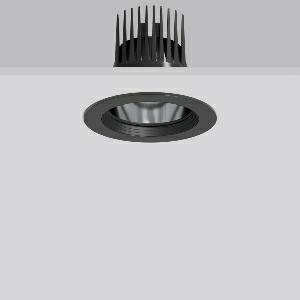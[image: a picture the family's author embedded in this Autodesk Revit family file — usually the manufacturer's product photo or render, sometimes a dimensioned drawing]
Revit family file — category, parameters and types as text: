
# Revit family: heledon_maxi_e_901756_003_8b9c
name_source: partatom
category: Lighting Fixtures
units: mm (PartAtom-declared; Revit-internal decimal feet)

## family parameters
Cut with Voids When Loaded = No
Host = Face
Light Source = No
Part Type = Normal
Room Calculation Point = No
Round Connector Dimension = Use Diameter
Shared = No

## types (1)
- HELEDON maxi E (1 x LED Modul 930, 3250 lm, 3000)
    Apparent Load = 25 VA
    Approval mark = CE
    CIE Flux Codes = 100 100 100 100 100
    Color Rendering = 90
    Color Temperature = 3000
    Default Elevation = 1800 mm
    Description = Series: HELEDON maxi
Round recessed downlight. Housing: die-cast aluminium, powder-coated. Black plastic ring and recessed LED to prevent glare from the side. Optical assembly with reflector made of MIRO-Silver with 98% total light reflection for outstanding efficiency - can be changed without tools. Best colour rendering index Ra>90. Suitable for Recessed ceiling mounting. Installation without tools thanks to spring fastening system. Including separate LED converter with connecting cable 600 mm.High quality converter without flickering and stroboscopic effect. Through-wiring box (5 pole) available as accessory. The following accessories can be mounted without use of tools: interchangeable lenses, decorative glasses, honeycomb louvre, clear and frosted diffusers, white interchangeable plastic ring. 
Colour: deep black, matt (RAL 9005)
Diameter: 162 mm
Height: 3 mm
Cut-out diameter: 152 mm
Recess height: 200 mm
Luminaire: recess height: 135 mm
Lamp: LED
Socket: without socket
Colour temperature: 3000K
Colour rendering index (CRI): 92
System power: 25 W
Rated luminous flux: 3250 lm
Luminous efficiency: 130 lm/W
Control gear: Regulated power supply
Protection class: II
Type of protection: IP 20
    Height = 0 mm  [stored 0 ft]
    Lamp = 1 x LED Modul 930
    Lamp Light Flux = 3250 lm
    Lamp count = 1
    Length = 162 mm
    Lifetime = 50000 h
    Luminous efficacy = 130 lm/W
    Manufacturer = RZB
    ModVariant = No
    Model = 901756.003
    Mounting Place = Ceiling
    Mounting Type = Recessed
    Number of Poles = 1
    OnlyDefault = Yes
    Power Factor = 1
    Product Name = HELEDON maxi E
    Product group = Recessed downlights
    ProductGroupID = 402
    Protection Class = Protection class II
    Protection Degree = IP 20
    RLX_Detail_Level = 1
    RLX_Emergency_Light_Flux = 0 lm
    RLX_Emergency_Type = 0
    RLX_Emergency_Type_DB = No
    RlxData = <blob elided: 121321 chars, md5=615be974>
    Socket = socket
    Standby Power = 0 W
    System Light Flux = 3250 lm
    System Power = 25 W
    Type Comments = Product without accessories
    Type Image = 901662.003.jpg
    URL = http://relux.com
    VarID = ---
    Voltage = 230 V
    Voltage Range = 220-240 V
    Weight = 0.00 kg
    Width = 0 mm  [stored 0 ft]

note: [stored X ft] marks values corroborated as IEEE doubles in the binary element streams (Revit-internal decimal feet)

## geometry (parser evidence)
native form markers: Blend x4, Sweep x11
no freeform markers — native parametric forms only
